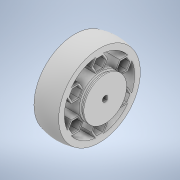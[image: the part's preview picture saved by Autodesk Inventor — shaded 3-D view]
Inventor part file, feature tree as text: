
AUTODESK INVENTOR PART (.ipt)
format: ipt  version: 2020 (Build 240168000, 168)  size: 298,496 bytes
history: native  units: in
note: dims shown in document units (in); Inventor stores cm internally (conversion verified against a paired STEP export)
features: sketch x4, extrude x2, revolve x2, projected_geometry x1
ambient origin geometry x8: Origin, YZ Plane, XZ Plane, XY Plane, X Axis, Y Axis, Z Axis, Center Point
bodies: Solid1 (feature_tree)
feature tree (9):
  extrude  "Extrusion1"  Depth=0.1181in
  sketch  "Sketch3"  dims[d6=0.8858in d7=0.1181in]
  revolve  "Revolution1"  [1 undecoded]
  extrude  "Extrusion2"  Depth=0.1181in
  revolve  "Revolution2"  [1 undecoded]
  sketch  "Sketch1"  dims[d0=0.1181in d1=0.0394in]
  sketch  "Sketch2"  dims[d3=1.6929in d4=0.1181in]
  projected_geometry  "Projected Loop1"
  sketch  "Sketch4"  dims[d8=0.0in d9=1.6929in d10=0.1181in d11=0.0315in d12=2.3622in d14=360.0deg d16=0.5118in d17=0.0in d19=90.0deg d20=0.0394in d22=60.0deg d24=0.0394in d25=90.0deg d26=60.0deg]
note: 2 required parameter values undecoded (feature->parameter linkage not recoverable at this tier; creation-order binding heuristic only, values carry confidence <= 0.55)
